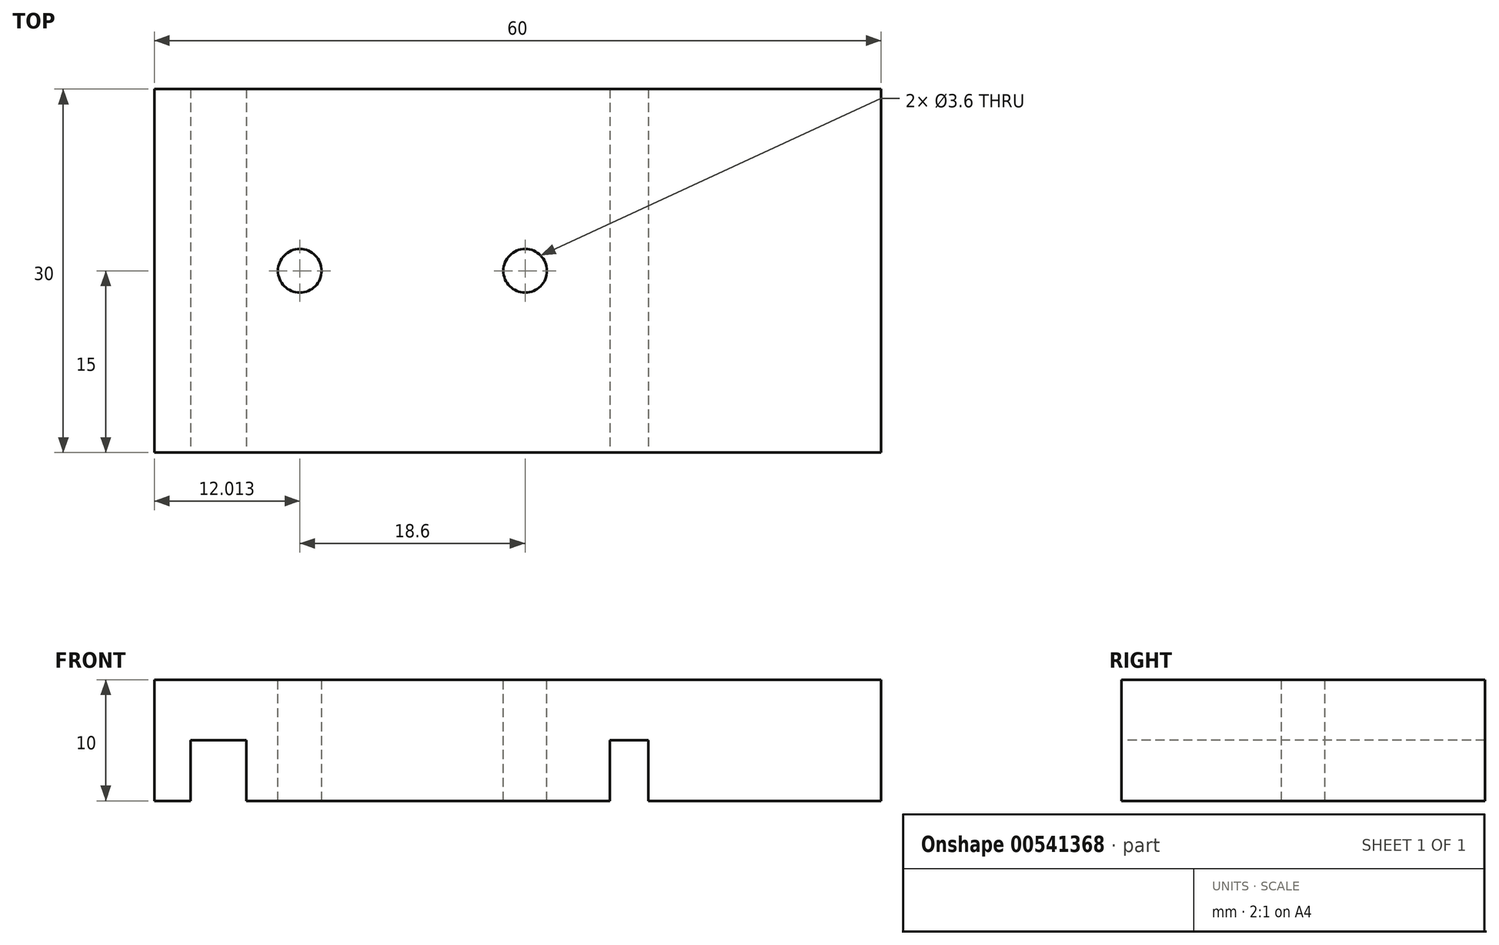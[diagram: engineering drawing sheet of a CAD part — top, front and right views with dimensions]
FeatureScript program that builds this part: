
annotation { "Feature Type Name" : "Feature", "Feature Type Description" : "" }
export const myFeature = defineFeature(function(context is Context, id is Id, definition is map)
    precondition{}
    {
        {
            var Q0;
            Q0=qCreatedBy(makeId("Top.planeOp"),FACE);
            var sketch = newSketch(context, id + "F0", { "sketchPlane" : qUnion([Q0])});
            skLineSegment(sketch, "E0.bottom", {"start": v(30, 15) * mm, "end": v(-30, 15) * mm});
            skLineSegment(sketch, "E0.top", {"start": v(30, -15) * mm, "end": v(-30, -15) * mm});
            skLineSegment(sketch, "E0.left", {"start": v(30, 15) * mm, "end": v(30, -15) * mm});
            skLineSegment(sketch, "E0.right", {"start": v(-30, 15) * mm, "end": v(-30, -15) * mm});
            skPoint(sketch, "E0.middle", {"position": v(0, 0) * mm});
            skSolve(sketch);
        }
        {
            var Q0;
            Q0 = qSketchRegion(id + "F0", true);
            extrude(context, id + "F1", {"entities" : qUnion([Q0]), "endBound" : BoundingType.SYMMETRIC, "depth" : 10 * mm, "offsetDistance" : 25 * mm});
        }
        {
            var Q0;
            Q0=makeQuery(id+"F1.opExtrude","CAP_FACE",FACE,{"disambiguationData":[OSD([sQuery(id+"F0.wireOp",EDGE,"E0.bottom"),sQuery(id+"F0.wireOp",EDGE,"E0.top"),sQuery(id+"F0.wireOp",EDGE,"E0.left"),sQuery(id+"F0.wireOp",EDGE,"E0.right")])],"isStart":true});
            var sketch = newSketch(context, id + "F2", { "sketchPlane" : qUnion([Q0])});
            skLineSegment(sketch, "E1.bottom", {"start": v(10.8, -15) * mm, "end": v(7.6, -15) * mm});
            skLineSegment(sketch, "E1.top", {"start": v(10.8, 15) * mm, "end": v(7.6, 15) * mm});
            skLineSegment(sketch, "E1.left", {"start": v(10.8, -15) * mm, "end": v(10.8, 15) * mm});
            skLineSegment(sketch, "E1.right", {"start": v(7.6, -15) * mm, "end": v(7.6, 15) * mm});
            skLineSegment(sketch, "E2.bottom", {"start": v(-22.4, -15) * mm, "end": v(-27, -15) * mm});
            skLineSegment(sketch, "E2.top", {"start": v(-22.4, 15) * mm, "end": v(-27, 15) * mm});
            skLineSegment(sketch, "E2.left", {"start": v(-22.4, -15) * mm, "end": v(-22.4, 15) * mm});
            skLineSegment(sketch, "E2.right", {"start": v(-27, -15) * mm, "end": v(-27, 15) * mm});
            skSolve(sketch);
        }
        {
            var Q0;
            Q0 = qSketchRegion(id + "F2", true);
            extrude(context, id + "F3", {"entities" : qUnion([Q0]), "operationType" : NewBodyOperationType.REMOVE, "oppositeDirection" : true, "depth" : 5 * mm, "offsetDistance" : 25 * mm});
        }
        {
            var Q0;
            Q0=makeQuery(id+"F1.opExtrude","CAP_FACE",FACE,{"disambiguationData":[OSD([sQuery(id+"F0.wireOp",EDGE,"E0.bottom"),sQuery(id+"F0.wireOp",EDGE,"E0.top"),sQuery(id+"F0.wireOp",EDGE,"E0.left"),sQuery(id+"F0.wireOp",EDGE,"E0.right")])],"isStart":false});
            var sketch = newSketch(context, id + "F4", { "sketchPlane" : qUnion([Q0])});
            skCircle(sketch, "E3", {"center": v(-17.99, 0) * mm, "radius": 1.8 * mm});
            skSolve(sketch);
        }
        {
            var Q0;
            Q0 = qSketchRegion(id + "F4", true);
            extrude(context, id + "F5", {"entities" : qUnion([Q0]), "operationType" : NewBodyOperationType.REMOVE, "oppositeDirection" : true, "depth" : 26 * mm, "offsetDistance" : 25 * mm});
        }
        {
            var Q0;
            Q0=makeQuery(id+"F1.opExtrude","CAP_FACE",FACE,{"disambiguationData":[OSD([sQuery(id+"F0.wireOp",EDGE,"E0.bottom"),sQuery(id+"F0.wireOp",EDGE,"E0.top"),sQuery(id+"F0.wireOp",EDGE,"E0.left"),sQuery(id+"F0.wireOp",EDGE,"E0.right")])],"isStart":false});
            var sketch = newSketch(context, id + "F6", { "sketchPlane" : qUnion([Q0])});
            skCircle(sketch, "E4", {"center": v(0.61, 0) * mm, "radius": 1.8 * mm});
            skSolve(sketch);
        }
        {
            var Q0;
            Q0 = qSketchRegion(id + "F6", true);
            extrude(context, id + "F7", {"entities" : qUnion([Q0]), "operationType" : NewBodyOperationType.REMOVE, "oppositeDirection" : true, "depth" : 26 * mm, "offsetDistance" : 25 * mm});
        }
    });
